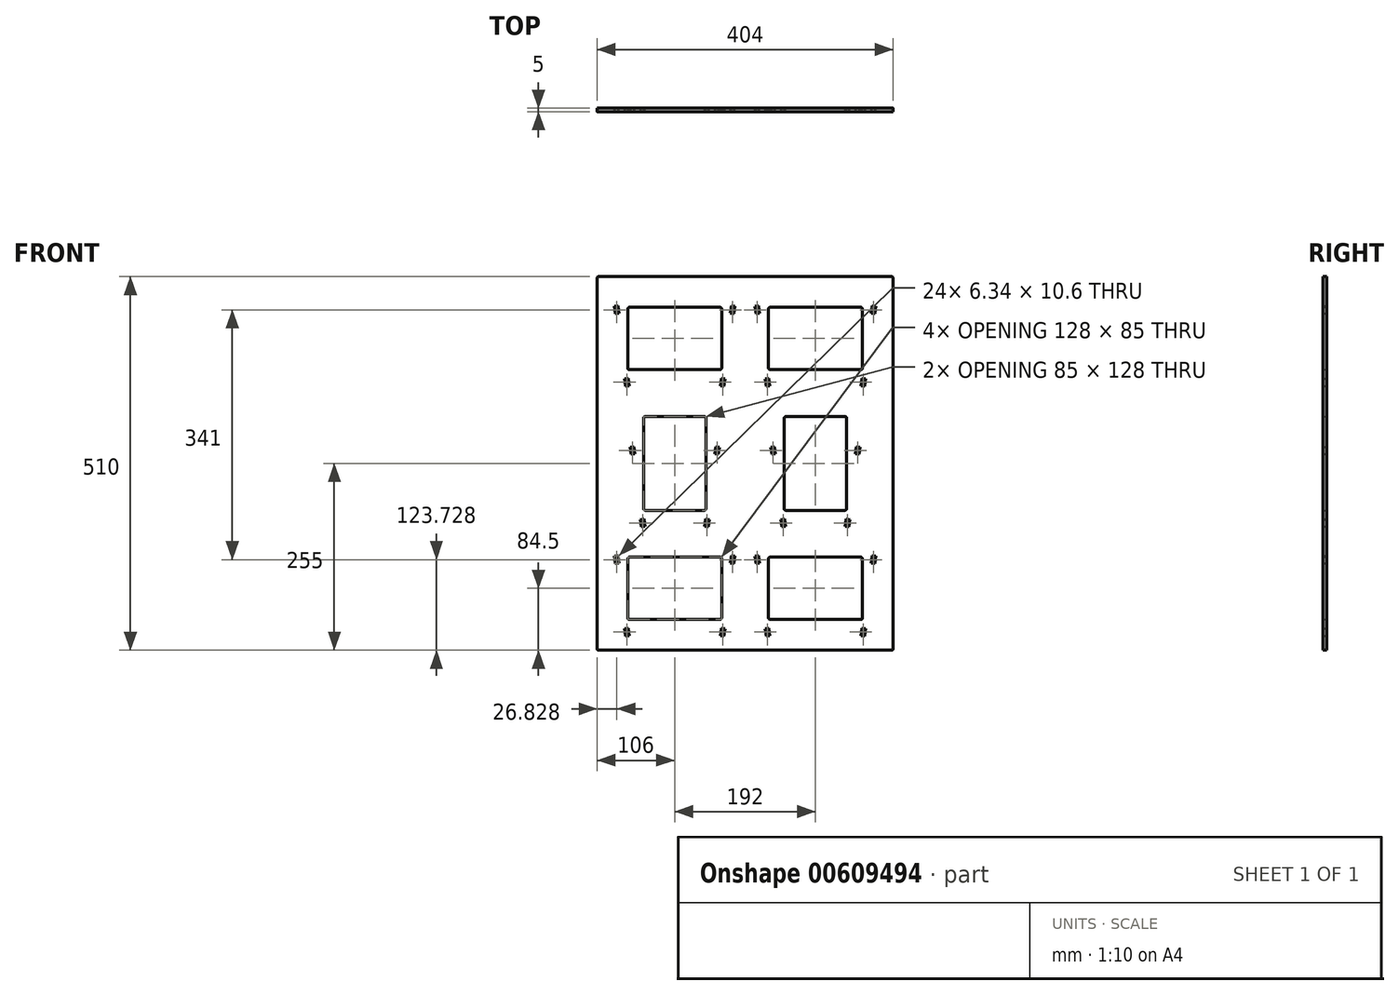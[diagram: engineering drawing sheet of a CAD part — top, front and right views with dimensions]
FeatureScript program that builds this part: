
annotation { "Feature Type Name" : "Feature", "Feature Type Description" : "" }
export const myFeature = defineFeature(function(context is Context, id is Id, definition is map)
    precondition{}
    {
        {
            var Q0;
            Q0=qCreatedBy(makeId("Front.planeOp"),FACE);
            var sketch = newSketch(context, id + "F0", { "sketchPlane" : qUnion([Q0])});
            skLineSegment(sketch, "E0.bottom", {"start": v(0, 0) * mm, "end": v(404, 0) * mm});
            skLineSegment(sketch, "E0.top", {"start": v(0, 510) * mm, "end": v(404, 510) * mm});
            skLineSegment(sketch, "E0.left", {"start": v(0, 0) * mm, "end": v(0, 510) * mm});
            skLineSegment(sketch, "E0.right", {"start": v(404, 0) * mm, "end": v(404, 510) * mm});
            skLineSegment(sketch, "E1.bottom", {"start": v(30, 30) * mm, "end": v(182, 30) * mm});
            skLineSegment(sketch, "E1.top", {"start": v(30, 139) * mm, "end": v(182, 139) * mm});
            skLineSegment(sketch, "E1.left", {"start": v(30, 30) * mm, "end": v(30, 139) * mm});
            skLineSegment(sketch, "E1.right", {"start": v(182, 30) * mm, "end": v(182, 139) * mm});
            skLineSegment(sketch, "E2.bottom", {"start": v(222, 30) * mm, "end": v(374, 30) * mm});
            skLineSegment(sketch, "E2.top", {"start": v(222, 139) * mm, "end": v(374, 139) * mm});
            skLineSegment(sketch, "E2.left", {"start": v(222, 30) * mm, "end": v(222, 139) * mm});
            skLineSegment(sketch, "E2.right", {"start": v(374, 30) * mm, "end": v(374, 139) * mm});
            skLineSegment(sketch, "E3.bottom", {"start": v(51.5, 179) * mm, "end": v(160.5, 179) * mm});
            skLineSegment(sketch, "E3.top", {"start": v(51.5, 331) * mm, "end": v(160.5, 331) * mm});
            skLineSegment(sketch, "E3.left", {"start": v(51.5, 179) * mm, "end": v(51.5, 331) * mm});
            skLineSegment(sketch, "E3.right", {"start": v(160.5, 179) * mm, "end": v(160.5, 331) * mm});
            skLineSegment(sketch, "E4.bottom", {"start": v(243.5, 179) * mm, "end": v(352.5, 179) * mm});
            skLineSegment(sketch, "E4.top", {"start": v(243.5, 331) * mm, "end": v(352.5, 331) * mm});
            skLineSegment(sketch, "E4.left", {"start": v(243.5, 179) * mm, "end": v(243.5, 331) * mm});
            skLineSegment(sketch, "E4.right", {"start": v(352.5, 179) * mm, "end": v(352.5, 331) * mm});
            skLineSegment(sketch, "E5.bottom", {"start": v(30, 371) * mm, "end": v(182, 371) * mm});
            skLineSegment(sketch, "E5.top", {"start": v(30, 480) * mm, "end": v(182, 480) * mm});
            skLineSegment(sketch, "E5.left", {"start": v(30, 371) * mm, "end": v(30, 480) * mm});
            skLineSegment(sketch, "E5.right", {"start": v(182, 371) * mm, "end": v(182, 480) * mm});
            skLineSegment(sketch, "E6.bottom", {"start": v(222, 371) * mm, "end": v(374, 371) * mm});
            skLineSegment(sketch, "E6.top", {"start": v(222, 480) * mm, "end": v(374, 480) * mm});
            skLineSegment(sketch, "E6.left", {"start": v(222, 371) * mm, "end": v(222, 480) * mm});
            skLineSegment(sketch, "E6.right", {"start": v(374, 371) * mm, "end": v(374, 480) * mm});
            skLineSegment(sketch, "E7.bottom", {"start": v(235.92, 20.1) * mm, "end": v(230.97, 19.4) * mm});
            skLineSegment(sketch, "E7.top", {"start": v(234.53, 30) * mm, "end": v(229.57, 29.3) * mm});
            skLineSegment(sketch, "E7.left", {"start": v(235.92, 20.1) * mm, "end": v(234.53, 30) * mm});
            skLineSegment(sketch, "E7.right", {"start": v(230.97, 19.4) * mm, "end": v(229.57, 29.3) * mm});
            skLineSegment(sketch, "E8.bottom", {"start": v(217.05, 118.43) * mm, "end": v(222, 119.12) * mm});
            skLineSegment(sketch, "E8.top", {"start": v(215.66, 128.33) * mm, "end": v(220.6, 129.03) * mm});
            skLineSegment(sketch, "E8.left", {"start": v(217.05, 118.43) * mm, "end": v(215.66, 128.33) * mm});
            skLineSegment(sketch, "E8.right", {"start": v(222, 119.12) * mm, "end": v(220.6, 129.03) * mm});
            skLineSegment(sketch, "E9.bottom", {"start": v(365.03, 19.4) * mm, "end": v(360.08, 20.1) * mm});
            skLineSegment(sketch, "E9.top", {"start": v(366.43, 29.3) * mm, "end": v(361.47, 30) * mm});
            skLineSegment(sketch, "E9.left", {"start": v(365.03, 19.4) * mm, "end": v(366.43, 29.3) * mm});
            skLineSegment(sketch, "E9.right", {"start": v(360.08, 20.1) * mm, "end": v(361.47, 30) * mm});
            skLineSegment(sketch, "E10.bottom", {"start": v(374, 119.12) * mm, "end": v(378.95, 118.43) * mm});
            skLineSegment(sketch, "E10.top", {"start": v(375.4, 129.03) * mm, "end": v(380.34, 128.33) * mm});
            skLineSegment(sketch, "E10.left", {"start": v(374, 119.12) * mm, "end": v(375.4, 129.03) * mm});
            skLineSegment(sketch, "E10.right", {"start": v(378.95, 118.43) * mm, "end": v(380.34, 128.33) * mm});
            skLineSegment(sketch, "E11.0", {"start": v(229.57, 29.3) * mm, "end": v(234.53, 30) * mm, "construction": true});
            skLineSegment(sketch, "E11.1", {"start": v(234.53, 30) * mm, "end": v(222, 119.12) * mm, "construction": true});
            skLineSegment(sketch, "E12.0", {"start": v(361.47, 30) * mm, "end": v(366.43, 29.3) * mm, "construction": true});
            skLineSegment(sketch, "E12.1", {"start": v(366.43, 29.3) * mm, "end": v(378.95, 118.43) * mm, "construction": true});
            skLineSegment(sketch, "E13.bottom", {"start": v(43.92, 20.1) * mm, "end": v(38.97, 19.4) * mm});
            skLineSegment(sketch, "E13.top", {"start": v(42.53, 30) * mm, "end": v(37.57, 29.3) * mm});
            skLineSegment(sketch, "E13.left", {"start": v(43.92, 20.1) * mm, "end": v(42.53, 30) * mm});
            skLineSegment(sketch, "E13.right", {"start": v(38.97, 19.4) * mm, "end": v(37.57, 29.3) * mm});
            skLineSegment(sketch, "E14.bottom", {"start": v(25.05, 118.43) * mm, "end": v(30, 119.12) * mm});
            skLineSegment(sketch, "E14.top", {"start": v(23.66, 128.33) * mm, "end": v(28.6, 129.03) * mm});
            skLineSegment(sketch, "E14.left", {"start": v(25.05, 118.43) * mm, "end": v(23.66, 128.33) * mm});
            skLineSegment(sketch, "E14.right", {"start": v(30, 119.12) * mm, "end": v(28.6, 129.03) * mm});
            skLineSegment(sketch, "E15.bottom", {"start": v(173.03, 19.4) * mm, "end": v(168.08, 20.1) * mm});
            skLineSegment(sketch, "E15.top", {"start": v(174.43, 29.3) * mm, "end": v(169.47, 30) * mm});
            skLineSegment(sketch, "E15.left", {"start": v(173.03, 19.4) * mm, "end": v(174.43, 29.3) * mm});
            skLineSegment(sketch, "E15.right", {"start": v(168.08, 20.1) * mm, "end": v(169.47, 30) * mm});
            skLineSegment(sketch, "E16.bottom", {"start": v(182, 119.12) * mm, "end": v(186.95, 118.43) * mm});
            skLineSegment(sketch, "E16.top", {"start": v(183.4, 129.03) * mm, "end": v(188.34, 128.33) * mm});
            skLineSegment(sketch, "E16.left", {"start": v(182, 119.12) * mm, "end": v(183.4, 129.03) * mm});
            skLineSegment(sketch, "E16.right", {"start": v(186.95, 118.43) * mm, "end": v(188.34, 128.33) * mm});
            skLineSegment(sketch, "E17.0", {"start": v(29.02, 28.1) * mm, "end": v(37.57, 29.3) * mm, "construction": true});
            skLineSegment(sketch, "E18.0", {"start": v(166.6, 30.4) * mm, "end": v(169.47, 30) * mm, "construction": true});
            skLineSegment(sketch, "E19.bottom", {"start": v(235.92, 361.1) * mm, "end": v(230.97, 360.4) * mm});
            skLineSegment(sketch, "E19.top", {"start": v(234.53, 371) * mm, "end": v(229.57, 370.3) * mm});
            skLineSegment(sketch, "E19.left", {"start": v(235.92, 361.1) * mm, "end": v(234.53, 371) * mm});
            skLineSegment(sketch, "E19.right", {"start": v(230.97, 360.4) * mm, "end": v(229.57, 370.3) * mm});
            skLineSegment(sketch, "E20.bottom", {"start": v(217.05, 459.43) * mm, "end": v(222, 460.12) * mm});
            skLineSegment(sketch, "E20.top", {"start": v(215.66, 469.33) * mm, "end": v(220.6, 470.03) * mm});
            skLineSegment(sketch, "E20.left", {"start": v(217.05, 459.43) * mm, "end": v(215.66, 469.33) * mm});
            skLineSegment(sketch, "E20.right", {"start": v(222, 460.12) * mm, "end": v(220.6, 470.03) * mm});
            skLineSegment(sketch, "E21.bottom", {"start": v(365.03, 360.4) * mm, "end": v(360.08, 361.1) * mm});
            skLineSegment(sketch, "E21.top", {"start": v(366.43, 370.3) * mm, "end": v(361.47, 371) * mm});
            skLineSegment(sketch, "E21.left", {"start": v(365.03, 360.4) * mm, "end": v(366.43, 370.3) * mm});
            skLineSegment(sketch, "E21.right", {"start": v(360.08, 361.1) * mm, "end": v(361.47, 371) * mm});
            skLineSegment(sketch, "E22.bottom", {"start": v(374, 460.12) * mm, "end": v(378.95, 459.43) * mm});
            skLineSegment(sketch, "E22.top", {"start": v(375.4, 470.03) * mm, "end": v(380.34, 469.33) * mm});
            skLineSegment(sketch, "E22.left", {"start": v(374, 460.12) * mm, "end": v(375.4, 470.03) * mm});
            skLineSegment(sketch, "E22.right", {"start": v(378.95, 459.43) * mm, "end": v(380.34, 469.33) * mm});
            skLineSegment(sketch, "E23.0", {"start": v(229.57, 370.3) * mm, "end": v(234.2, 370.95) * mm, "construction": true});
            skLineSegment(sketch, "E24.0", {"start": v(361.47, 371) * mm, "end": v(366.76, 370.26) * mm, "construction": true});
            skLineSegment(sketch, "E25.bottom", {"start": v(43.92, 361.1) * mm, "end": v(38.97, 360.4) * mm});
            skLineSegment(sketch, "E25.top", {"start": v(42.53, 371) * mm, "end": v(37.57, 370.3) * mm});
            skLineSegment(sketch, "E25.left", {"start": v(43.92, 361.1) * mm, "end": v(42.53, 371) * mm});
            skLineSegment(sketch, "E25.right", {"start": v(38.97, 360.4) * mm, "end": v(37.57, 370.3) * mm});
            skLineSegment(sketch, "E26.bottom", {"start": v(25.05, 459.43) * mm, "end": v(30, 460.12) * mm});
            skLineSegment(sketch, "E26.top", {"start": v(23.66, 469.33) * mm, "end": v(28.6, 470.03) * mm});
            skLineSegment(sketch, "E26.left", {"start": v(25.05, 459.43) * mm, "end": v(23.66, 469.33) * mm});
            skLineSegment(sketch, "E26.right", {"start": v(30, 460.12) * mm, "end": v(28.6, 470.03) * mm});
            skLineSegment(sketch, "E27.bottom", {"start": v(173.03, 360.4) * mm, "end": v(168.08, 361.1) * mm});
            skLineSegment(sketch, "E27.top", {"start": v(174.43, 370.3) * mm, "end": v(169.47, 371) * mm});
            skLineSegment(sketch, "E27.left", {"start": v(173.03, 360.4) * mm, "end": v(174.43, 370.3) * mm});
            skLineSegment(sketch, "E27.right", {"start": v(168.08, 361.1) * mm, "end": v(169.47, 371) * mm});
            skLineSegment(sketch, "E28.bottom", {"start": v(182, 460.12) * mm, "end": v(186.95, 459.43) * mm});
            skLineSegment(sketch, "E28.top", {"start": v(183.4, 470.03) * mm, "end": v(188.34, 469.33) * mm});
            skLineSegment(sketch, "E28.left", {"start": v(182, 460.12) * mm, "end": v(183.4, 470.03) * mm});
            skLineSegment(sketch, "E28.right", {"start": v(186.95, 459.43) * mm, "end": v(188.34, 469.33) * mm});
            skLineSegment(sketch, "E29.0", {"start": v(166.94, 371.36) * mm, "end": v(169.47, 371) * mm, "construction": true});
            skLineSegment(sketch, "E30.bottom", {"start": v(257.42, 169.1) * mm, "end": v(252.47, 168.4) * mm});
            skLineSegment(sketch, "E30.top", {"start": v(256.03, 179) * mm, "end": v(251.07, 178.3) * mm});
            skLineSegment(sketch, "E30.left", {"start": v(257.42, 169.1) * mm, "end": v(256.03, 179) * mm});
            skLineSegment(sketch, "E30.right", {"start": v(252.47, 168.4) * mm, "end": v(251.07, 178.3) * mm});
            skLineSegment(sketch, "E31.bottom", {"start": v(238.55, 267.43) * mm, "end": v(243.5, 268.12) * mm});
            skLineSegment(sketch, "E31.top", {"start": v(237.16, 277.33) * mm, "end": v(242.1, 278.03) * mm});
            skLineSegment(sketch, "E31.left", {"start": v(238.55, 267.43) * mm, "end": v(237.16, 277.33) * mm});
            skLineSegment(sketch, "E31.right", {"start": v(243.5, 268.12) * mm, "end": v(242.1, 278.03) * mm});
            skLineSegment(sketch, "E32.bottom", {"start": v(343.53, 168.4) * mm, "end": v(338.58, 169.1) * mm});
            skLineSegment(sketch, "E32.top", {"start": v(344.93, 178.3) * mm, "end": v(339.97, 179) * mm});
            skLineSegment(sketch, "E32.left", {"start": v(343.53, 168.4) * mm, "end": v(344.93, 178.3) * mm});
            skLineSegment(sketch, "E32.right", {"start": v(338.58, 169.1) * mm, "end": v(339.97, 179) * mm});
            skLineSegment(sketch, "E33.bottom", {"start": v(352.5, 268.12) * mm, "end": v(357.45, 267.43) * mm});
            skLineSegment(sketch, "E33.top", {"start": v(353.9, 278.03) * mm, "end": v(358.84, 277.33) * mm});
            skLineSegment(sketch, "E33.left", {"start": v(352.5, 268.12) * mm, "end": v(353.9, 278.03) * mm});
            skLineSegment(sketch, "E33.right", {"start": v(357.45, 267.43) * mm, "end": v(358.84, 277.33) * mm});
            skLineSegment(sketch, "E34.0", {"start": v(221.33, 174.12) * mm, "end": v(251.07, 178.3) * mm, "construction": true});
            skLineSegment(sketch, "E35.0", {"start": v(339.97, 179) * mm, "end": v(371.12, 174.62) * mm, "construction": true});
            skLineSegment(sketch, "E36.bottom", {"start": v(65.42, 169.1) * mm, "end": v(60.47, 168.4) * mm});
            skLineSegment(sketch, "E36.top", {"start": v(64.03, 179) * mm, "end": v(59.07, 178.3) * mm});
            skLineSegment(sketch, "E36.left", {"start": v(65.42, 169.1) * mm, "end": v(64.03, 179) * mm});
            skLineSegment(sketch, "E36.right", {"start": v(60.47, 168.4) * mm, "end": v(59.07, 178.3) * mm});
            skLineSegment(sketch, "E37.bottom", {"start": v(46.55, 267.43) * mm, "end": v(51.5, 268.12) * mm});
            skLineSegment(sketch, "E37.top", {"start": v(45.16, 277.33) * mm, "end": v(50.1, 278.03) * mm});
            skLineSegment(sketch, "E37.left", {"start": v(46.55, 267.43) * mm, "end": v(45.16, 277.33) * mm});
            skLineSegment(sketch, "E37.right", {"start": v(51.5, 268.12) * mm, "end": v(50.1, 278.03) * mm});
            skLineSegment(sketch, "E38.bottom", {"start": v(151.53, 168.4) * mm, "end": v(146.58, 169.1) * mm});
            skLineSegment(sketch, "E38.top", {"start": v(152.93, 178.3) * mm, "end": v(147.97, 179) * mm});
            skLineSegment(sketch, "E38.left", {"start": v(151.53, 168.4) * mm, "end": v(152.93, 178.3) * mm});
            skLineSegment(sketch, "E38.right", {"start": v(146.58, 169.1) * mm, "end": v(147.97, 179) * mm});
            skLineSegment(sketch, "E39.bottom", {"start": v(160.5, 268.12) * mm, "end": v(165.45, 267.43) * mm});
            skLineSegment(sketch, "E39.top", {"start": v(161.9, 278.03) * mm, "end": v(166.84, 277.33) * mm});
            skLineSegment(sketch, "E39.left", {"start": v(160.5, 268.12) * mm, "end": v(161.9, 278.03) * mm});
            skLineSegment(sketch, "E39.right", {"start": v(165.45, 267.43) * mm, "end": v(166.84, 277.33) * mm});
            skLineSegment(sketch, "E40.0", {"start": v(37.84, 175.32) * mm, "end": v(59.07, 178.3) * mm, "construction": true});
            skLineSegment(sketch, "E41.0", {"start": v(147.97, 179) * mm, "end": v(169.37, 176) * mm, "construction": true});
            skLineSegment(sketch, "E42.0", {"start": v(63.5, 191) * mm, "end": v(63.5, 319) * mm});
            skLineSegment(sketch, "E42.1", {"start": v(63.5, 191) * mm, "end": v(148.5, 191) * mm});
            skLineSegment(sketch, "E42.2", {"start": v(148.5, 191) * mm, "end": v(148.5, 319) * mm});
            skLineSegment(sketch, "E42.3", {"start": v(63.5, 319) * mm, "end": v(148.5, 319) * mm});
            skLineSegment(sketch, "E43.0", {"start": v(42, 127) * mm, "end": v(170, 127) * mm});
            skLineSegment(sketch, "E43.1", {"start": v(42, 42) * mm, "end": v(42, 127) * mm});
            skLineSegment(sketch, "E43.2", {"start": v(42, 42) * mm, "end": v(170, 42) * mm});
            skLineSegment(sketch, "E43.3", {"start": v(170, 42) * mm, "end": v(170, 127) * mm});
            skLineSegment(sketch, "E44.0", {"start": v(234, 127) * mm, "end": v(362, 127) * mm});
            skLineSegment(sketch, "E44.1", {"start": v(234, 42) * mm, "end": v(234, 127) * mm});
            skLineSegment(sketch, "E44.2", {"start": v(234, 42) * mm, "end": v(362, 42) * mm});
            skLineSegment(sketch, "E44.3", {"start": v(362, 42) * mm, "end": v(362, 127) * mm});
            skLineSegment(sketch, "E45.0", {"start": v(255.5, 319) * mm, "end": v(340.5, 319) * mm});
            skLineSegment(sketch, "E45.1", {"start": v(255.5, 191) * mm, "end": v(255.5, 319) * mm});
            skLineSegment(sketch, "E45.2", {"start": v(255.5, 191) * mm, "end": v(340.5, 191) * mm});
            skLineSegment(sketch, "E45.3", {"start": v(340.5, 191) * mm, "end": v(340.5, 319) * mm});
            skLineSegment(sketch, "E46.0", {"start": v(42, 468) * mm, "end": v(170, 468) * mm});
            skLineSegment(sketch, "E46.1", {"start": v(42, 383) * mm, "end": v(42, 468) * mm});
            skLineSegment(sketch, "E46.2", {"start": v(42, 383) * mm, "end": v(170, 383) * mm});
            skLineSegment(sketch, "E46.3", {"start": v(170, 383) * mm, "end": v(170, 468) * mm});
            skLineSegment(sketch, "E47.0", {"start": v(234, 468) * mm, "end": v(362, 468) * mm});
            skLineSegment(sketch, "E47.1", {"start": v(234, 383) * mm, "end": v(234, 468) * mm});
            skLineSegment(sketch, "E47.2", {"start": v(234, 383) * mm, "end": v(362, 383) * mm});
            skLineSegment(sketch, "E47.3", {"start": v(362, 383) * mm, "end": v(362, 468) * mm});
            skSolve(sketch);
        }
        {
            var Q0;
            Q0=makeQuery(id+"F0.imprint","IMPRINT",FACE,{"disambiguationData":[TD([[makeQuery(id+"F0.imprint","IMPRINT",EDGE,{"derivedFrom":sQuery(id+"F0.wireOp",EDGE,"E0.bottom")}),1.0]])]});
            var Q1;
            {var subQ1=sQuery(id+"F0.wireOp",EDGE,"E3.top");Q1=makeQuery(id+"F0.imprint","IMPRINT",FACE,{"disambiguationData":[TD([[makeQuery(id+"F0.imprint","IMPRINT",EDGE,{"derivedFrom":subQ1}),-1.0]])]});}
            var Q2;
            {var subQ1=sQuery(id+"F0.wireOp",EDGE,"E1.top");Q2=makeQuery(id+"F0.imprint","IMPRINT",FACE,{"disambiguationData":[TD([[makeQuery(id+"F0.imprint","IMPRINT",EDGE,{"derivedFrom":subQ1}),-1.0]])]});}
            var Q3;
            {var subQ1=sQuery(id+"F0.wireOp",EDGE,"E2.top");Q3=makeQuery(id+"F0.imprint","IMPRINT",FACE,{"disambiguationData":[TD([[makeQuery(id+"F0.imprint","IMPRINT",EDGE,{"derivedFrom":subQ1}),-1.0]])]});}
            var Q4;
            {var subQ1=sQuery(id+"F0.wireOp",EDGE,"E4.top");Q4=makeQuery(id+"F0.imprint","IMPRINT",FACE,{"disambiguationData":[TD([[makeQuery(id+"F0.imprint","IMPRINT",EDGE,{"derivedFrom":subQ1}),-1.0]])]});}
            var Q5;
            {var subQ1=sQuery(id+"F0.wireOp",EDGE,"E5.top");Q5=makeQuery(id+"F0.imprint","IMPRINT",FACE,{"disambiguationData":[TD([[makeQuery(id+"F0.imprint","IMPRINT",EDGE,{"derivedFrom":subQ1}),-1.0]])]});}
            var Q6;
            {var subQ1=sQuery(id+"F0.wireOp",EDGE,"E6.top");Q6=makeQuery(id+"F0.imprint","IMPRINT",FACE,{"disambiguationData":[TD([[makeQuery(id+"F0.imprint","IMPRINT",EDGE,{"derivedFrom":subQ1}),-1.0]])]});}
            extrude(context, id + "F1", {"entities" : qUnion([Q0, Q1, Q2, Q3, Q4, Q5, Q6]), "depth" : 5 * mm, "offsetDistance" : 25 * mm});
        }
        {
            var Q0;
            Q0=makeQuery(id+"F1.opExtrude","SWEPT_EDGE",EDGE,{"disambiguationData":[OSD([sQuery(id+"F0.wireOp",EDGE,"E0.top"),sQuery(id+"F0.wireOp",EDGE,"E0.left")])]});
            var Q1;
            Q1=makeQuery(id+"F1.opExtrude","SWEPT_EDGE",EDGE,{"disambiguationData":[OSD([sQuery(id+"F0.wireOp",EDGE,"E0.top"),sQuery(id+"F0.wireOp",EDGE,"E0.right")])]});
            var Q2;
            Q2=makeQuery(id+"F1.opExtrude","SWEPT_EDGE",EDGE,{"disambiguationData":[OSD([sQuery(id+"F0.wireOp",EDGE,"E0.bottom"),sQuery(id+"F0.wireOp",EDGE,"E0.left")])]});
            var Q3;
            Q3=makeQuery(id+"F1.opExtrude","SWEPT_EDGE",EDGE,{"disambiguationData":[OSD([sQuery(id+"F0.wireOp",EDGE,"E0.bottom"),sQuery(id+"F0.wireOp",EDGE,"E0.right")])]});
            var Q4;
            Q4=makeQuery(id+"F1.opExtrude","SWEPT_EDGE",EDGE,{"disambiguationData":[OSD([sQuery(id+"F0.wireOp",EDGE,"E44.0"),sQuery(id+"F0.wireOp",EDGE,"E44.1")])]});
            var Q5;
            Q5=makeQuery(id+"F1.opExtrude","SWEPT_EDGE",EDGE,{"disambiguationData":[OSD([sQuery(id+"F0.wireOp",EDGE,"E45.0"),sQuery(id+"F0.wireOp",EDGE,"E45.1")])]});
            var Q6;
            Q6=makeQuery(id+"F1.opExtrude","SWEPT_EDGE",EDGE,{"disambiguationData":[OSD([sQuery(id+"F0.wireOp",EDGE,"E42.0"),sQuery(id+"F0.wireOp",EDGE,"E42.3")])]});
            var Q7;
            Q7=makeQuery(id+"F1.opExtrude","SWEPT_EDGE",EDGE,{"disambiguationData":[OSD([sQuery(id+"F0.wireOp",EDGE,"E43.0"),sQuery(id+"F0.wireOp",EDGE,"E43.1")])]});
            var Q8;
            Q8=makeQuery(id+"F1.opExtrude","SWEPT_EDGE",EDGE,{"disambiguationData":[OSD([sQuery(id+"F0.wireOp",EDGE,"E47.0"),sQuery(id+"F0.wireOp",EDGE,"E47.1")])]});
            var Q9;
            Q9=makeQuery(id+"F1.opExtrude","SWEPT_EDGE",EDGE,{"disambiguationData":[OSD([sQuery(id+"F0.wireOp",EDGE,"E46.0"),sQuery(id+"F0.wireOp",EDGE,"E46.1")])]});
            var Q10;
            Q10=makeQuery(id+"F1.opExtrude","SWEPT_EDGE",EDGE,{"disambiguationData":[OSD([sQuery(id+"F0.wireOp",EDGE,"E46.0"),sQuery(id+"F0.wireOp",EDGE,"E46.3")])]});
            var Q11;
            Q11=makeQuery(id+"F1.opExtrude","SWEPT_EDGE",EDGE,{"disambiguationData":[OSD([sQuery(id+"F0.wireOp",EDGE,"E47.0"),sQuery(id+"F0.wireOp",EDGE,"E47.3")])]});
            var Q12;
            Q12=makeQuery(id+"F1.opExtrude","SWEPT_EDGE",EDGE,{"disambiguationData":[OSD([sQuery(id+"F0.wireOp",EDGE,"E45.0"),sQuery(id+"F0.wireOp",EDGE,"E45.3")])]});
            var Q13;
            Q13=makeQuery(id+"F1.opExtrude","SWEPT_EDGE",EDGE,{"disambiguationData":[OSD([sQuery(id+"F0.wireOp",EDGE,"E42.2"),sQuery(id+"F0.wireOp",EDGE,"E42.3")])]});
            var Q14;
            Q14=makeQuery(id+"F1.opExtrude","SWEPT_EDGE",EDGE,{"disambiguationData":[OSD([sQuery(id+"F0.wireOp",EDGE,"E43.0"),sQuery(id+"F0.wireOp",EDGE,"E43.3")])]});
            var Q15;
            Q15=makeQuery(id+"F1.opExtrude","SWEPT_EDGE",EDGE,{"disambiguationData":[OSD([sQuery(id+"F0.wireOp",EDGE,"E44.0"),sQuery(id+"F0.wireOp",EDGE,"E44.3")])]});
            var Q16;
            Q16=makeQuery(id+"F1.opExtrude","SWEPT_EDGE",EDGE,{"disambiguationData":[OSD([sQuery(id+"F0.wireOp",EDGE,"E44.2"),sQuery(id+"F0.wireOp",EDGE,"E44.3")])]});
            var Q17;
            Q17=makeQuery(id+"F1.opExtrude","SWEPT_EDGE",EDGE,{"disambiguationData":[OSD([sQuery(id+"F0.wireOp",EDGE,"E43.2"),sQuery(id+"F0.wireOp",EDGE,"E43.3")])]});
            var Q18;
            Q18=makeQuery(id+"F1.opExtrude","SWEPT_EDGE",EDGE,{"disambiguationData":[OSD([sQuery(id+"F0.wireOp",EDGE,"E42.1"),sQuery(id+"F0.wireOp",EDGE,"E42.2")])]});
            var Q19;
            Q19=makeQuery(id+"F1.opExtrude","SWEPT_EDGE",EDGE,{"disambiguationData":[OSD([sQuery(id+"F0.wireOp",EDGE,"E45.2"),sQuery(id+"F0.wireOp",EDGE,"E45.3")])]});
            var Q20;
            Q20=makeQuery(id+"F1.opExtrude","SWEPT_EDGE",EDGE,{"disambiguationData":[OSD([sQuery(id+"F0.wireOp",EDGE,"E46.2"),sQuery(id+"F0.wireOp",EDGE,"E46.3")])]});
            var Q21;
            Q21=makeQuery(id+"F1.opExtrude","SWEPT_EDGE",EDGE,{"disambiguationData":[OSD([sQuery(id+"F0.wireOp",EDGE,"E47.2"),sQuery(id+"F0.wireOp",EDGE,"E47.3")])]});
            var Q22;
            Q22=makeQuery(id+"F1.opExtrude","SWEPT_EDGE",EDGE,{"disambiguationData":[OSD([sQuery(id+"F0.wireOp",EDGE,"E43.1"),sQuery(id+"F0.wireOp",EDGE,"E43.2")])]});
            var Q23;
            Q23=makeQuery(id+"F1.opExtrude","SWEPT_EDGE",EDGE,{"disambiguationData":[OSD([sQuery(id+"F0.wireOp",EDGE,"E44.1"),sQuery(id+"F0.wireOp",EDGE,"E44.2")])]});
            var Q24;
            Q24=makeQuery(id+"F1.opExtrude","SWEPT_EDGE",EDGE,{"disambiguationData":[OSD([sQuery(id+"F0.wireOp",EDGE,"E45.1"),sQuery(id+"F0.wireOp",EDGE,"E45.2")])]});
            var Q25;
            Q25=makeQuery(id+"F1.opExtrude","SWEPT_EDGE",EDGE,{"disambiguationData":[OSD([sQuery(id+"F0.wireOp",EDGE,"E42.0"),sQuery(id+"F0.wireOp",EDGE,"E42.1")])]});
            var Q26;
            Q26=makeQuery(id+"F1.opExtrude","SWEPT_EDGE",EDGE,{"disambiguationData":[OSD([sQuery(id+"F0.wireOp",EDGE,"E46.1"),sQuery(id+"F0.wireOp",EDGE,"E46.2")])]});
            var Q27;
            Q27=makeQuery(id+"F1.opExtrude","SWEPT_EDGE",EDGE,{"disambiguationData":[OSD([sQuery(id+"F0.wireOp",EDGE,"E47.1"),sQuery(id+"F0.wireOp",EDGE,"E47.2")])]});
            fillet(context, id + "F2", {"entities" : qUnion([Q0, Q1, Q2, Q3, Q4, Q5, Q6, Q7, Q8, Q9, Q10, Q11, Q12, Q13, Q14, Q15, Q16, Q17, Q18, Q19, Q20, Q21, Q22, Q23, Q24, Q25, Q26, Q27]), "radius" : 2 * mm, "tangentPropagation" : true, "allowEdgeOverflow" : false});
        }
    });
